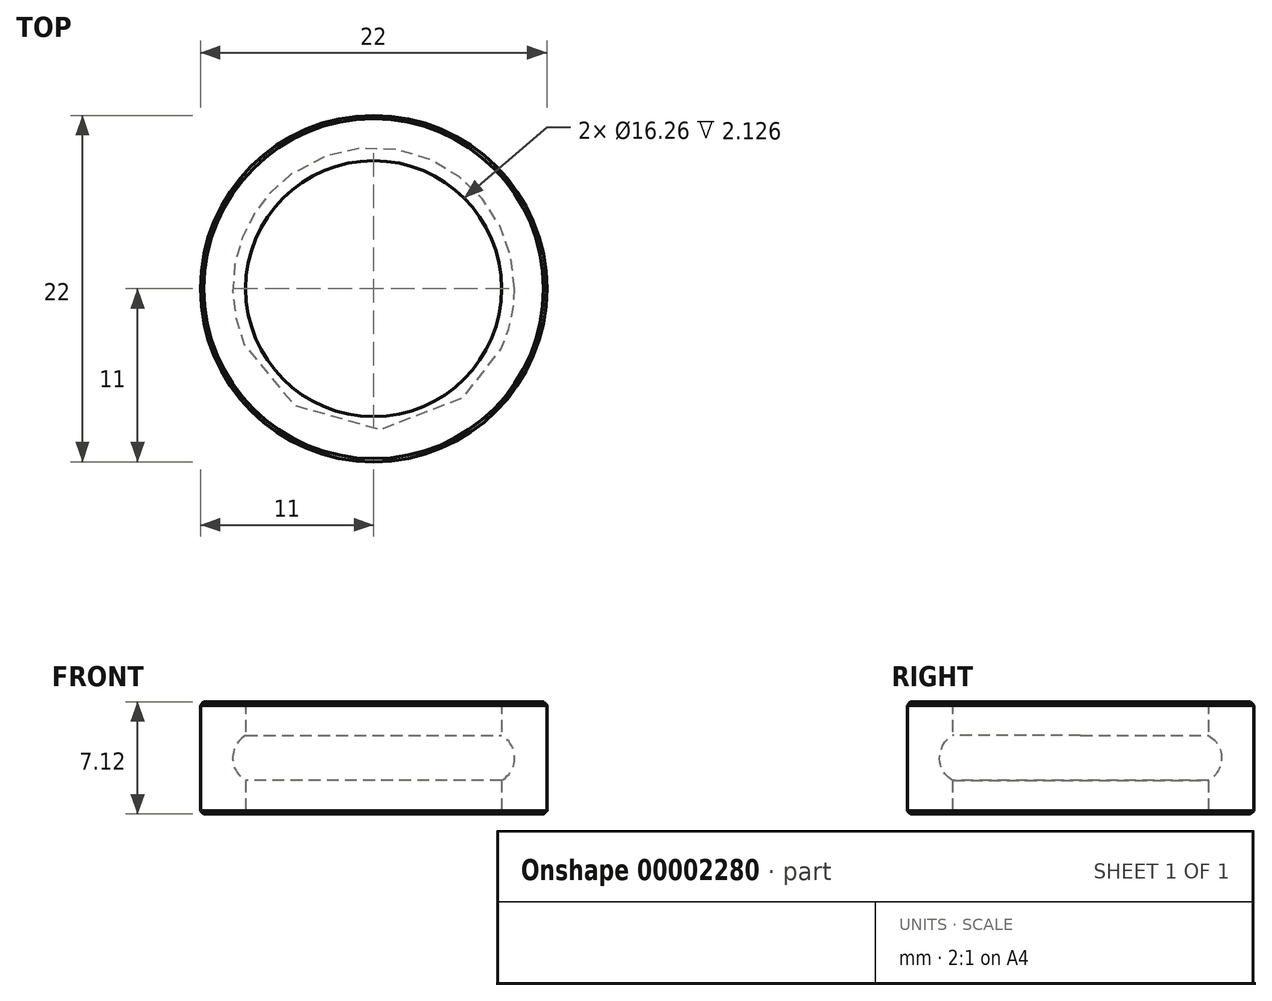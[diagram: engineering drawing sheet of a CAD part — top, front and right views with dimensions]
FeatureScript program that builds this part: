
annotation { "Feature Type Name" : "Feature", "Feature Type Description" : "" }
export const myFeature = defineFeature(function(context is Context, id is Id, definition is map)
    precondition{}
    {
        {
            var Q0;
            Q0=qCreatedBy(makeId("Top.planeOp"),FACE);
            var sketch = newSketch(context, id + "F0", { "sketchPlane" : qUnion([Q0])});
            skCircle(sketch, "E0", {"center": v(0, 0) * mm, "radius": 11 * mm});
            skCircle(sketch, "E1", {"center": v(0, 0) * mm, "radius": 8.13 * mm});
            skSolve(sketch);
        }
        {
            var Q0;
            Q0=makeQuery(id+"F0.imprint","IMPRINT",FACE,{"disambiguationData":[TD([[makeQuery(id+"F0.imprint","IMPRINT",EDGE,{"derivedFrom":sQuery(id+"F0.wireOp",EDGE,"E0")}),1.0]])]});
            extrude(context, id + "F1", {"entities" : qUnion([Q0]), "endBound" : BoundingType.SYMMETRIC, "depth" : 7.11 * mm});
        }
        {
            var Q0;
            Q0=makeQuery(id+"F1.opExtrude","CAP_EDGE",EDGE,{"disambiguationData":[OSD([sQuery(id+"F0.wireOp",EDGE,"E0")])],"isStart":false});
            var Q1;
            Q1=makeQuery(id+"F1.opExtrude","CAP_EDGE",EDGE,{"disambiguationData":[OSD([sQuery(id+"F0.wireOp",EDGE,"E0")])],"isStart":true});
            chamfer(context, id + "F2", {"entities" : qUnion([Q0, Q1]), "width" : 0.2 * mm, "tangentPropagation" : true});
        }
        {
            var Q0;
            Q0=qCreatedBy(makeId("Right.planeOp"),FACE);
            var sketch = newSketch(context, id + "F3", { "sketchPlane" : qUnion([Q0])});
            skArc(sketch, "E2", {"start": v(7.3, -1.65) * mm, "mid": v(8.95, 0) * mm, "end": v(7.3, 1.65) * mm});
            skLineSegment(sketch, "E3", {"start": v(7.3, 1.65) * mm, "end": v(7.3, -1.65) * mm});
            skLineSegment(sketch, "E4", {"start": v(0, 0) * mm, "end": v(0, 4.16) * mm, "construction": true});
            skSolve(sketch);
        }
        {
            var Q0;
            Q0=makeQuery(id+"F3.imprint","IMPRINT",FACE,{"disambiguationData":[TD([[makeQuery(id+"F3.imprint","IMPRINT",EDGE,{"derivedFrom":sQuery(id+"F3.wireOp",EDGE,"E2")}),1.0]])]});
            var Q1;
            Q1=sQuery(id+"F3.wireOp",EDGE,"E2");
            var Q2;
            Q2=sQuery(id+"F3.wireOp",EDGE,"E3");
            var Q3;
            Q3=sQuery(id+"F3.wireOp",EDGE,"E4");
            revolve(context, id + "F4", {"operationType" : NewBodyOperationType.REMOVE, "entities" : qUnion([Q0]), "surfaceEntities" : qUnion([Q1, Q2]), "axis" : qUnion([Q3]), "revolveType" : RevolveType.FULL, "oppositeDirection" : true});
        }
    });
